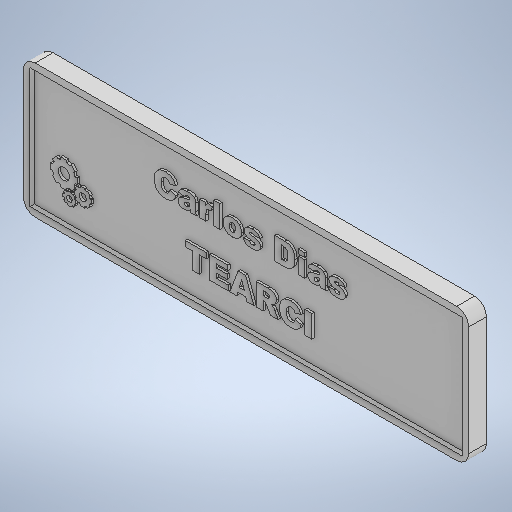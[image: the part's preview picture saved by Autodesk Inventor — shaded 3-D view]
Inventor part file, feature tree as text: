
AUTODESK INVENTOR PART (.ipt)
format: ipt  version: 2025.2 (Build 292293000, 293)  size: 889,344 bytes
history: native  units: mm
features: extrude x7, sketch x7, fillet x6, other x1
ambient origin geometry x8: Origin, YZ Plane, XZ Plane, XY Plane, X Axis, Y Axis, Z Axis, Center Point
bodies: Solid1 (feature_tree)
feature tree (21):
  extrude  "Extrusion1"  Depth=30.0mm
  extrude  "Extrusion2"  Depth=100.0mm
  fillet  "Face Fillet1"
  fillet  "Face Fillet2"
  fillet  "Face Fillet3"
  fillet  "Face Fillet4"
  fillet  "Face Fillet5"
  fillet  "Face Fillet6"
  extrude  "Extrusion3"  Depth=30.0mm
  extrude  "Extrusion4"  Depth=1.0mm TaperAngle=0.0deg
  extrude  "Extrusion5"  Depth=0.5mm
  extrude  "Extrusion6"  Depth=2.68mm
  extrude  "Extrusion7"  Depth=2.68mm
  sketch  "Sketch1"  dims[d0=100.0mm d1=30.0mm]
  sketch  "Sketch2"  dims[d2=3.0mm d3=0.0mm d4=100.0mm]
  sketch  "Sketch4"  dims[d5=30.0mm d6=97.0mm]
  other  "Image2"
  sketch  "Sketch6"  dims[d10=0.397mm d11=0.5mm]
  sketch  "Sketch7"  dims[d12=2.68mm d13=2.68mm]
  sketch  "Sketch8"  dims[d14=2.68mm d15=2.68mm d46=0.5mm d47=0.0mm d65=0.5mm d66=0.0mm d69=10.0mm d71=10.0mm d72=0.5mm d73=0.0mm d74=20.0mm d75=0.0mm d76=20.0mm d77=0.0mm d80=0.5mm d81=0.872665mm d82=0.5mm d83=0.872665mm]
  sketch  "Sketch5"  dims[d7=27.0mm d8=1.0mm d9=0.0mm]
